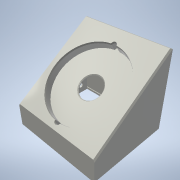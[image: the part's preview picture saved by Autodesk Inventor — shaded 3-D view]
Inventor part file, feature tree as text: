
AUTODESK INVENTOR PART (.ipt)
format: ipt  version: 2022.3 (Build 263350000, 350)  size: 257,536 bytes
history: native  units: mm
features: extrude x8, other x4, fillet x2, pattern_circular x1, chamfer x1, projected_geometry x1
ambient origin geometry x8: Origin, YZ Plane, XZ Plane, XY Plane, X Axis, Y Axis, Z Axis, Center Point
bodies: Solid1 (feature_tree)
feature tree (17):
  other  "XZ_master"
  extrude  "Walls_bottom"  Depth=105.0mm
  fillet  "Fillet2"  Radius=95.0mm
  other  "Profile"
  extrude  "Lip recess"  Depth=2.0mm
  fillet  "Lip_fillet"  Radius=25.0mm
  pattern_circular  "Circular Pattern1"  [2 undecoded]
  other  "Angled_top_face"
  extrude  "Walls_to_workplane"  Depth=1.2mm
  other  "Top_face"
  extrude  "Face"  Depth=2.0mm
  extrude  "Button_recess"  Depth=151.5mm TaperAngle=0.0deg
  extrude  "Side_cable_cutout"  Depth=21.816616mm
  extrude  "Recess_walls"  Depth=101.0mm TaperAngle=0.0deg
  extrude  "Recess_floor"  Depth=20.0mm TaperAngle=360.0deg
  chamfer  "Button_cutout_chamfer"  Distance=88.0mm
  projected_geometry  "Projected Loop1"
note: 2 required parameter values undecoded (feature->parameter linkage not recoverable at this tier; creation-order binding heuristic only, values carry confidence <= 0.55)
